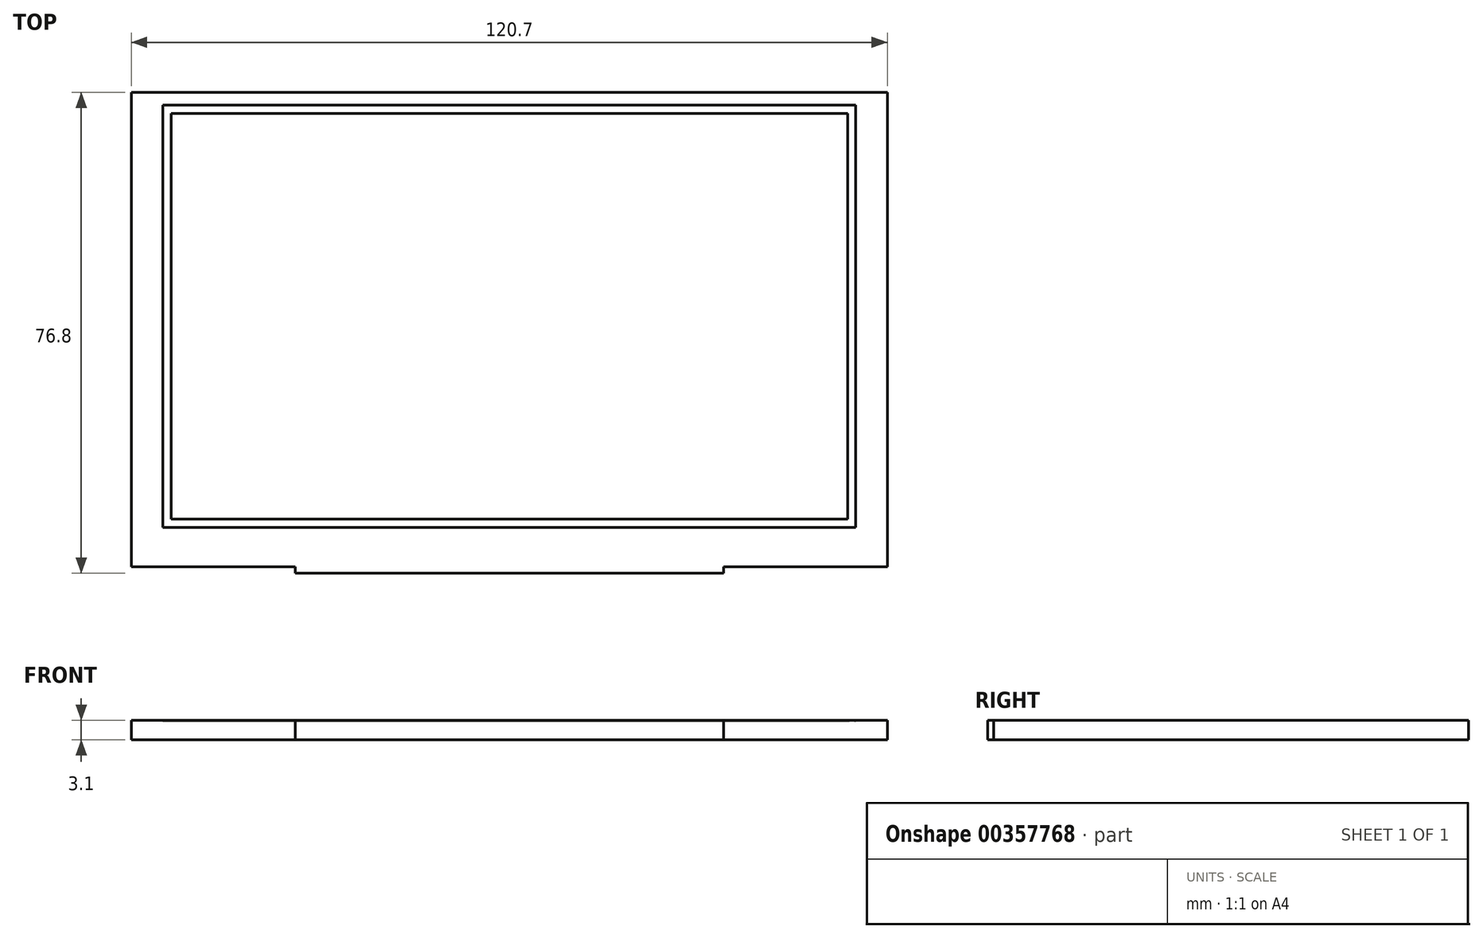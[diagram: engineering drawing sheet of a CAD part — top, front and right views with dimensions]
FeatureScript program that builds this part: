
annotation { "Feature Type Name" : "Feature", "Feature Type Description" : "" }
export const myFeature = defineFeature(function(context is Context, id is Id, definition is map)
    precondition{}
    {
        {
            var Q0;
            Q0=qCreatedBy(makeId("Top.planeOp"),FACE);
            var sketch = newSketch(context, id + "F0", { "sketchPlane" : qUnion([Q0])});
            skLineSegment(sketch, "E0.bottom", {"start": v(-60.35, 37.9) * mm, "end": v(60.35, 37.9) * mm});
            skLineSegment(sketch, "E0.top", {"start": v(-60.35, -37.9) * mm, "end": v(60.35, -37.9) * mm});
            skLineSegment(sketch, "E0.left", {"start": v(-60.35, 37.9) * mm, "end": v(-60.35, -37.9) * mm});
            skLineSegment(sketch, "E0.right", {"start": v(60.35, 37.9) * mm, "end": v(60.35, -37.9) * mm});
            skLineSegment(sketch, "E1", {"start": v(-60.35, 0) * mm, "end": v(0, 0) * mm, "construction": true});
            skLineSegment(sketch, "E2", {"start": v(0, 37.9) * mm, "end": v(0, 0) * mm, "construction": true});
            skSolve(sketch);
        }
        {
            var Q0;
            Q0=makeQuery(id+"F0.imprint","IMPRINT",FACE,{"disambiguationData":[TD([[makeQuery(id+"F0.imprint","IMPRINT",EDGE,{"derivedFrom":sQuery(id+"F0.wireOp",EDGE,"E0.bottom")}),-1.0]])]});
            extrude(context, id + "F1", {"entities" : qUnion([Q0]), "depth" : 3.1 * mm});
        }
        {
            var Q0;
            Q0=makeQuery(id+"F1.opExtrude","CAP_FACE",FACE,{"disambiguationData":[OSD([sQuery(id+"F0.wireOp",EDGE,"E0.bottom"),sQuery(id+"F0.wireOp",EDGE,"E0.top"),sQuery(id+"F0.wireOp",EDGE,"E0.left"),sQuery(id+"F0.wireOp",EDGE,"E0.right")])],"isStart":false});
            var sketch = newSketch(context, id + "F2", { "sketchPlane" : qUnion([Q0])});
            skLineSegment(sketch, "E3.bottom", {"start": v(-55.3, 35.83) * mm, "end": v(55.3, 35.83) * mm});
            skLineSegment(sketch, "E3.top", {"start": v(-55.3, -31.57) * mm, "end": v(55.3, -31.57) * mm});
            skLineSegment(sketch, "E3.left", {"start": v(-55.3, 35.83) * mm, "end": v(-55.3, -31.57) * mm});
            skLineSegment(sketch, "E3.right", {"start": v(55.3, 35.83) * mm, "end": v(55.3, -31.57) * mm});
            skLineSegment(sketch, "E4.0", {"start": v(-54, 34.53) * mm, "end": v(54, 34.53) * mm});
            skLineSegment(sketch, "E4.1", {"start": v(-54, 34.53) * mm, "end": v(-54, -30.27) * mm});
            skLineSegment(sketch, "E4.2", {"start": v(-54, -30.27) * mm, "end": v(54, -30.27) * mm});
            skLineSegment(sketch, "E4.3", {"start": v(54, 34.53) * mm, "end": v(54, -30.27) * mm});
            skSolve(sketch);
        }
        {
            var Q0;
            Q0=qSketchRegion(id+"F2",true);
            extrude(context, id + "F3", {"entities" : qUnion([Q0]), "operationType" : NewBodyOperationType.REMOVE, "oppositeDirection" : true, "depth" : 0.1 * mm});
        }
        {
            var Q0;
            Q0=makeQuery(id+"F1.opExtrude","SWEPT_FACE",FACE,{"disambiguationData":[OSD([sQuery(id+"F0.wireOp",EDGE,"E0.top")])]});
            var sketch = newSketch(context, id + "F4", { "sketchPlane" : qUnion([Q0])});
            skLineSegment(sketch, "E5.bottom", {"start": v(-34.2, 3.1) * mm, "end": v(34.19, 3.1) * mm});
            skLineSegment(sketch, "E5.top", {"start": v(-34.2, 0) * mm, "end": v(34.19, 0) * mm});
            skLineSegment(sketch, "E5.left", {"start": v(-34.2, 3.1) * mm, "end": v(-34.2, 0) * mm});
            skLineSegment(sketch, "E5.right", {"start": v(34.19, 3.1) * mm, "end": v(34.19, 0) * mm});
            skSolve(sketch);
        }
        {
            var Q0;
            Q0=qSketchRegion(id+"F4",true);
            extrude(context, id + "F5", {"entities" : qUnion([Q0]), "operationType" : NewBodyOperationType.ADD, "depth" : 1 * mm});
        }
    });
